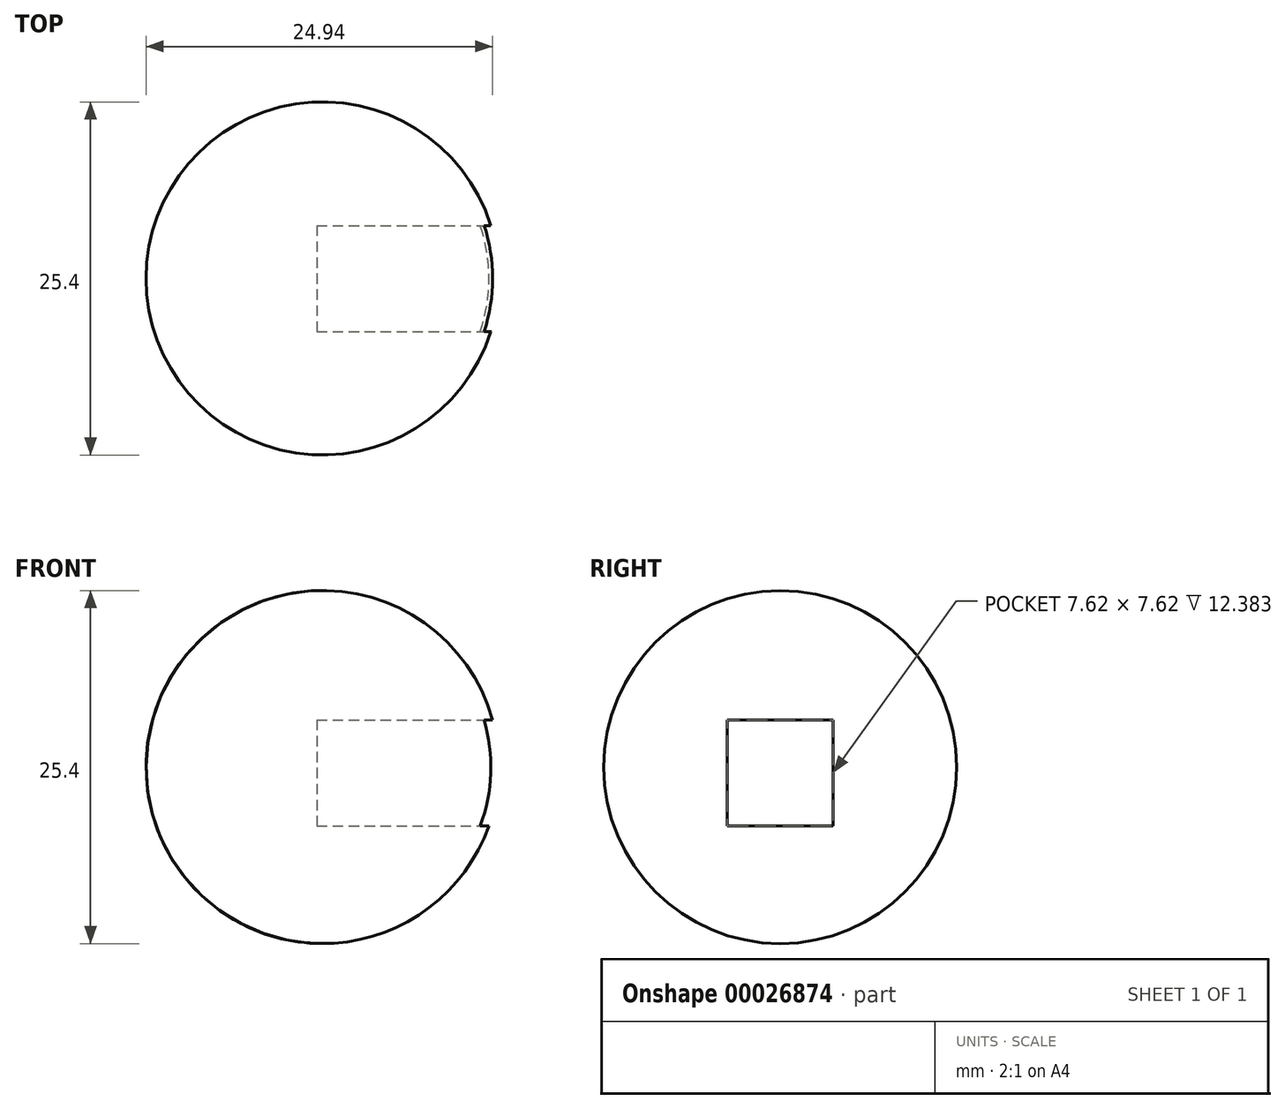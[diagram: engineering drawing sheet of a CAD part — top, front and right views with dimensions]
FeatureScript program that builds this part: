
annotation { "Feature Type Name" : "Feature", "Feature Type Description" : "" }
export const myFeature = defineFeature(function(context is Context, id is Id, definition is map)
    precondition{}
    {
        {
            var Q0;
            Q0=qCreatedBy(makeId("Front.planeOp"),FACE);
            var sketch = newSketch(context, id + "F0", { "sketchPlane" : qUnion([Q0])});
            skCircle(sketch, "E0", {"center": v(-33.82, 41.57) * mm, "radius": 12.7 * mm});
            skLineSegment(sketch, "E1", {"start": v(-34.65, 54.24) * mm, "end": v(-33, 28.9) * mm});
            skSolve(sketch);
        }
        {
            var Q0;
            {var subQ0=sQuery(id+"F0.wireOp",EDGE,"E1");Q0=makeQuery(id+"F0.imprint","IMPRINT",FACE,{"disambiguationData":[TD([[makeQuery(id+"F0.imprint","IMPRINT",EDGE,{"derivedFrom":subQ0}),1.0]])]});}
            var Q1;
            Q1=sQuery(id+"F0.wireOp",EDGE,"E1");
            revolve(context, id + "F1", {"entities" : qUnion([Q0]), "axis" : qUnion([Q1]), "revolveType" : RevolveType.FULL});
        }
        {
            var Q0;
            Q0=qCreatedBy(makeId("Right.planeOp"),FACE);
            var sketch = newSketch(context, id + "F2", { "sketchPlane" : qUnion([Q0])});
            skLineSegment(sketch, "E2.bottom", {"start": v(3.8, 44.96) * mm, "end": v(-3.81, 44.96) * mm});
            skLineSegment(sketch, "E2.top", {"start": v(3.8, 37.34) * mm, "end": v(-3.81, 37.34) * mm});
            skLineSegment(sketch, "E2.left", {"start": v(3.8, 44.96) * mm, "end": v(3.8, 37.34) * mm});
            skLineSegment(sketch, "E2.right", {"start": v(-3.81, 44.96) * mm, "end": v(-3.81, 37.34) * mm});
            skSolve(sketch);
        }
        {
            var Q0;
            Q0 = qSketchRegion(id + "F2", true);
            extrude(context, id + "F3", {"entities" : qUnion([Q0]), "operationType" : NewBodyOperationType.REMOVE, "endBound" : BoundingType.SYMMETRIC, "oppositeDirection" : true, "depth" : 68.48 * mm});
        }
    });
